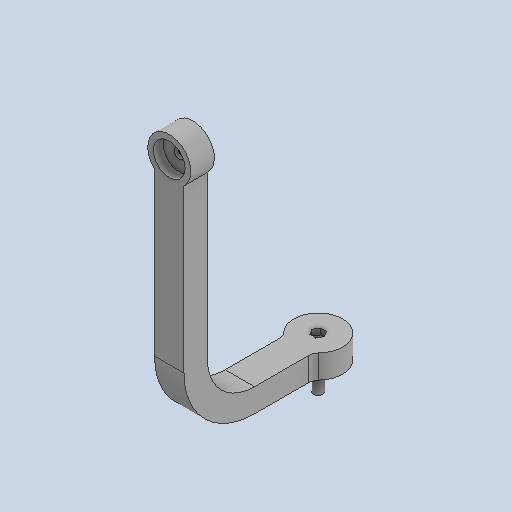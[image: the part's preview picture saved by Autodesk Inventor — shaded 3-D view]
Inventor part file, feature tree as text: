
AUTODESK INVENTOR PART (.ipt)
format: ipt  version: 2024 (Build 280153000, 153)  size: 332,800 bytes
history: native  units: mm
features: sketch x9, extrude x7, other x3, sweep x1, plane x1, mirror x1
ambient origin geometry x8: Origin, YZ Plane, XZ Plane, XY Plane, X Axis, Y Axis, Z Axis, Center Point
bodies: Solid1 (feature_tree)
feature tree (22):
  extrude  "Extrusion1"  Depth=12.0mm TaperAngle=0.0deg
  sweep  "Sweep2"
  plane  "Work Plane11"
  extrude  "Extrusion17"  TaperAngle=90.0deg  [1 undecoded]
  extrude  "Extrusion18"  TaperAngle=0.0deg  [1 undecoded]
  other  "Work Point1"
  extrude  "Extrusion20"  Depth=12.0mm TaperAngle=0.0deg
  extrude  "Extrusion21"  TaperAngle=0.0deg  [1 undecoded]
  mirror  "Mirror2"
  extrude  "Extrusion22"  Depth=10.0mm
  extrude  "Extrusion23"  Depth=26.0mm TaperAngle=0.0deg
  sketch  "Sketch1"  dims[d0=25.0mm d1=12.0mm d2=0.0mm]
  sketch  "Sketch22"  dims[d109=5.0mm d110=50.0mm]
  sketch  "Sketch23"  dims[d111=108.79758mm d112=90.0deg]
  sketch  "Sketch24"  dims[d113=30.0mm d114=0.0mm d115=0.0mm]
  sketch  "Sketch25"  dims[d116=-6.0mm d121=12.0mm d122=0.0mm]
  other  "Work Axis1"
  other  "Work Axis2"
  sketch  "Sketch27"  dims[d123=5.0mm d124=0.0mm d125=0.0mm]
  sketch  "Sketch28"  dims[d129=15.0mm d131=10.0mm]
  sketch  "Sketch29"  dims[d136=4.8mm d137=26.0mm d138=0.0mm]
  sketch  "Sketch30"  dims[d139=22.0mm d140=12.0mm d141=15.0mm d142=16.2mm d143=5.0mm d144=0.0mm d145=5.5mm d146=3.0mm d147=0.0mm d148=3.2mm d149=0.0mm d150=0.0mm d74=0.5mm d75=0.872665mm d76=0.5mm d77=0.872665mm d98=0.0mm d99=0.0mm d100=0.0mm d101=0.0mm d102=0.872665mm d103=0.5mm d104=0.872665mm]
note: 3 required parameter values undecoded (feature->parameter linkage not recoverable at this tier; creation-order binding heuristic only, values carry confidence <= 0.55)
